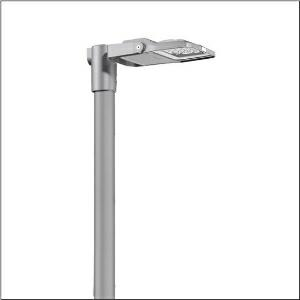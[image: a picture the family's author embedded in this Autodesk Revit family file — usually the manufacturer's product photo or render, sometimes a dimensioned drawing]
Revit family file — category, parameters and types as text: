
# Revit family: floodlight_fl_21_micro___pl61_5xa7761a4c3a_11fd
name_source: partatom
category: Lighting Fixtures
units: mm (PartAtom-declared; Revit-internal decimal feet)

## family parameters
Cut with Voids When Loaded = No
Host = Face
Light Source = No
Part Type = Normal
Room Calculation Point = No
Round Connector Dimension = Use Diameter
Shared = No

## types (1)
- --- (1 x LED, 3030 lm, 23.1 W, 4000K)
    Apparent Load = 23 VA
    CIE Flux Codes = 33 65 98 100 100
    Color Rendering = 70
    Color Temperature = 4000K
    Default Elevation = 1800 mm
    Description = Floodlight FL 21 micro, floodlight, primary light control with lens, of PMMA, primary optical cover: protective disc, of toughened safety glass, transparent, light distribution: PL61, light emission: direct distribution, installation type: surface-mounted, LED, High Power LED, rated luminous flux: 3.030lm, luminous efficacy: 131lm/W, light colour: 740, colour temperature: 4000K, control gear: ECG iQ, control: optimised constant luminous flux control (CLO 2.0), Desk-Remote (wireless, voltage-free reading and setting of iQ features in the workshop via application-optimized NFC function/RFID function), Light-Fading, Smart-Wire, Night-Set, Lumen-Switch, Temp-Guard, Auto-Match, with terminal, 6-pole, mains connection: 220..240V, AC, 50/60Hz, start of lifetime: 23W, end of lifetime: 24W, reduction: 11W, luminaire housing, of diecast aluminium, powder-coated, Siteco® metallic grey (DB 702S), corrosivity category C5 according to DIN EN ISO 12944, mast bracket, of steel, galvanised, powder-coated, Siteco® metallic grey (DB 702S), protection rating (complete): IP66, insulation class (complete): insulation class II (safety insulation), certification: CE, protection symbol: D, impact resistance: IK07, permissible operating ambient temperature: -40..+40°C, permissible operating ambient temperature for outdoor applications: -40..+50°C, standard: DIN EN 12944, packaging unit: 1 piece

Light Distribution: PL61
    Height = 65 mm
    Lamp = 1 x LED
    Lamp Light Flux = 3030 lm
    Lamp Power = 23.1 W
    Lamp count = 1
    Length = 312 mm
    Luminous efficacy = 131 lm/W
    Manufacturer = Siteco
    ModVariant = No
    Model = 5XA7761A4C3A
    Number of Poles = 1
    OnlyDefault = Yes
    Power Factor = 1
    Product Name = Floodlight FL 21 micro | PL61
    Product group = floodlight | pylon top
    ProductGroupID = 6101
    Protection Class = Protection class II
    Protection Degree = IP 66
    RLX_Detail_Level = 1
    RlxData = <blob elided: 101625 chars, md5=4dbe94eb>
    Socket = socket
    Standby Power = 0 W
    System Light Flux = 3030 lm
    System Power = 23 W
    Type Comments = factory setting: luminous flux: 100 % | dim-lin: 254 | 455 mA
    Type Image = l_1007121.jpg
    URL = http://relux.com
    VarID = @adj_115435
    Voltage = 0 V
    Weight = 0.00 kg
    Width = 230 mm

## geometry (parser evidence)
native form markers: Blend x4, Sweep x11
no freeform markers — native parametric forms only
